# Revit family: SGD-50
name_source: partatom
category: Lighting Fixtures
revit_build: Autodesk Revit 2014 (Build: 20130308_1515(x64)
units: mm (PartAtom-declared; Revit-internal decimal feet)

## types (2) — shared parameters
Apparent Load = 60 VA
Assembly Code = D5020200
Certifications = Listed to UL1598 for use in wet locations
Connector Description = Lighting Connector
Default Elevation = 48 "
Description = SLING FAMILY - DUSK TO DAWN
Features = Multi-purpose dusk-to-dawn LED luminare provides general purpose
area, security, roadway and landscape lighting
• Low profile housing with zero uplight design for environmentally
friendly installations
• Includes arm and photocontrol for automatic off during daylight hours
• Clamp for 1-5/8 inch to 2-3/8 inch diameter pipe
Housing Material = Paint - Hubbell - Metallic Bronze Textured
IP Rating = IP65
Lamp = LED
Length = 48 "
Load Classification = Lighting
Manufacturer = Hubbell Outdoor Lighting
Model = SGD-50
Power Factor = 1
Reflector Finish = Hubbell - White Glass
URL = https://www.hubbell.com
Voltage = 120 V
Warranty = 5 years Warranty
Wattage Comments = 60W
Watts = 60 W
Width = 11.63 "
Width 1 = 5 "

## per-type parameters (varying)
| type | Head | Pole |
| SGD-40-4K | SGD : SGD-40 | Paint - Hubbell - Metallic Bronze Textured |
| SGD-60-4K | SGD : SGD-60 | <By Category> |

## geometry (parser evidence)
native form markers: Sweep x5
no freeform markers — native parametric forms only
